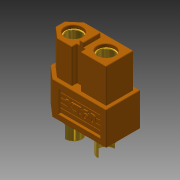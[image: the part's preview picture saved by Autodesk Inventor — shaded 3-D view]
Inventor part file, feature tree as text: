
AUTODESK INVENTOR PART (.ipt)
format: ipt  version: 2013 (Build 170138000, 138)  size: 743,936 bytes
history: native  units: mm
features: sketch x12, extrude x10, other x6, plane x4, projected_geometry x4, fillet x3, hole x1, mirror x1
ambient origin geometry x8: Origin, YZ Plane, XZ Plane, XY Plane, X Axis, Y Axis, Z Axis, Center Point
bodies: Volumenkörper1 (feature_tree)
feature tree (41):
  extrude  "Extrusion1"  Depth=8.0mm
  extrude  "Extrusion2"  Depth=3.0mm
  extrude  "Extrusion3"  Depth=3.0mm
  extrude  "Extrusion4"  Depth=0.8mm
  extrude  "Extrusion5"  Depth=1.2mm
  plane  "Arbeitsebene1"
  extrude  "Extrusion6"  TaperAngle=0.0deg  [1 undecoded]
  plane  "Arbeitsebene2"
  extrude  "Extrusion7"  Depth=4.0mm
  extrude  "Extrusion8"  Depth=8.0mm TaperAngle=0.0deg
  hole  "Bohrung1"  [1 undecoded]
  sketch  "Skizze10"  dims[d21=1.0mm d22=0.0mm d23=6.0mm]
  extrude  "Extrusion9"  Depth=6.0mm
  extrude  "Extrusion10"  Depth=4.0mm TaperAngle=0.0deg
  plane  "Arbeitsebene3"
  other  "Prägen1"
  mirror  "Spiegeln1"
  plane  "Arbeitsebene5"
  other  "Prägen2"
  fillet  "Rundung1"  [1 undecoded]
  fillet  "Rundung2"  Radius=3.5mm
  fillet  "Rundung3"  Radius=3.5mm
  sketch  "Skizze1"  dims[d0=15.6mm d1=8.0mm]
  sketch  "Skizze2"  dims[d2=2.6mm d3=3.0mm]
  sketch  "Skizze3"  dims[d4=2.6mm d5=3.0mm]
  sketch  "Skizze4"  dims[d6=7.8mm d7=0.0mm d8=0.8mm]
  sketch  "Skizze5"  dims[d9=2.0mm d10=1.2mm]
  sketch  "Skizze6"  dims[d11=6.0mm d12=0.0mm]
  sketch  "Skizze7"  dims[d13=8.0mm d14=0.0mm d15=4.0mm]
  sketch  "Skizze8"  dims[d16=4.0mm d17=8.0mm d18=0.0mm]
  projected_geometry  "Projizierte Kontur1"
  projected_geometry  "Projizierte Kontur2"
  projected_geometry  "Projizierte Kontur3"
  sketch  "Skizze9"  dims[d19=1.1mm d20=4.0mm]
  projected_geometry  "Projizierte Kontur4"
  sketch  "Skizze11"  dims[d24=6.0mm d25=4.0mm d26=0.0mm d27=-0.8mm d28=3.5mm d29=3.5mm]
  sketch  "Skizze15"  dims[d30=20.0mm d31=0.0mm d32=-3.5mm d33=2.0mm d34=0.0mm d35=2.0mm d36=3.0mm d37=2.0mm d38=3.0mm d39=1.0mm d40=0.0mm d41=3.5mm d42=6.0mm d43=4.0mm d44=2.0mm d45=90.0deg d46=0.4mm d47=20.594885mm d48=9.8mm d49=5.2mm d50=0.52mm d51=50.0mm d53=1.04mm d54=10.0mm d56=10.0mm d58=0.5mm d59=0.0mm d60=0.6mm d61=0.0mm d62=-0.4mm d63=7.0mm d66=1.4mm d67=2.0mm d68=0.3mm d69=0.0mm d78=-0.4mm d79=7.0mm d80=2.01mm d81=1.4mm d82=0.3mm d83=0.0mm d84=0.2mm d85=0.2mm d86=0.2mm]
  other  "Schnittkanten projizieren1"
  other  "Schnittkanten projizieren2"
  other  "Schnittkanten projizieren3"
  other  "Schnittkanten projizieren4"
note: 3 required parameter values undecoded (feature->parameter linkage not recoverable at this tier; creation-order binding heuristic only, values carry confidence <= 0.55)
